# Revit family: Shower_Wall_Abey_BuildersShowers_MiniDual_FaceBased
name_source: partatom
category: Plumbing Fixtures
units: mm (PartAtom-declared; Revit-internal decimal feet)

## family parameters
Cut with Voids When Loaded = Yes
Host = Face
Maintain Annotation Orientation = No
OmniClass Number = 23.31.17.00
OmniClass Title = Showers
Part Type = Normal
Room Calculation Point = No
Round Connector Dimension = Use Diameter
Shared = No

## types (3) — shared parameters
Assembly Code = D2010710
CW Connection = Yes
Default Elevation = 1,500 mm
HW Connection = Yes
IfcExportAs = IfcSanitaryTerminal
IfcExportType = SHOWER
Manufacturer = Abey
ManufacturerOverallDepth = 515 mm
ManufacturerOverallHeight = 417 mm
ManufacturerOverallWidth = 250 mm
ManufacturerURLProductSpecific = https://www.abeyspecifier.com.au
ModifiedIssue = 20251103 $
URL = https://www.abey.com.au
Uniclass2015Code = Pr_40_20_87_76
Uniclass2015Title = Shower heads
Uniclass2015Version = Products v1.38
Vent Connection = No
Waste Connection = No
zero-valued in all types: Cost

## per-type parameters (varying)
| type | Description | ManufacturerSpecCode | Material | Model | Type Comments |
| Chrome (AB-MDS) | Abey Builders 304 Stainless Steel Mini Dual Shower Set Shower Head 3 Function Handheld Chrome | AB-MDS | Metal_Abey_Chrome | AB-MDS | Shower - Wall - Mini Dual - Chrome |
| Brushed Nickel (AB-MDS-BN) | Abey Builders 304 Stainless Steel Mini Dual Shower Set Shower Head 3 Function Handheld Brushed Nickel | AB-MDS-BN | Metal_Abey_BrushedNickel | AB-MDS-BN | Shower - Wall - Mini Dual - Brushed Nickel |
| Black (AB-MDS-B) | Abey Builders 304 Stainless Steel Mini Dual Shower Set Shower Head 3 Function Handheld Black | AB-MDS-B | Metal_Abey_Black | AB-MDS-B | Shower - Wall - Mini Dual - Black |

## geometry (parser evidence)
native form markers: Sweep x4
no freeform markers — native parametric forms only
